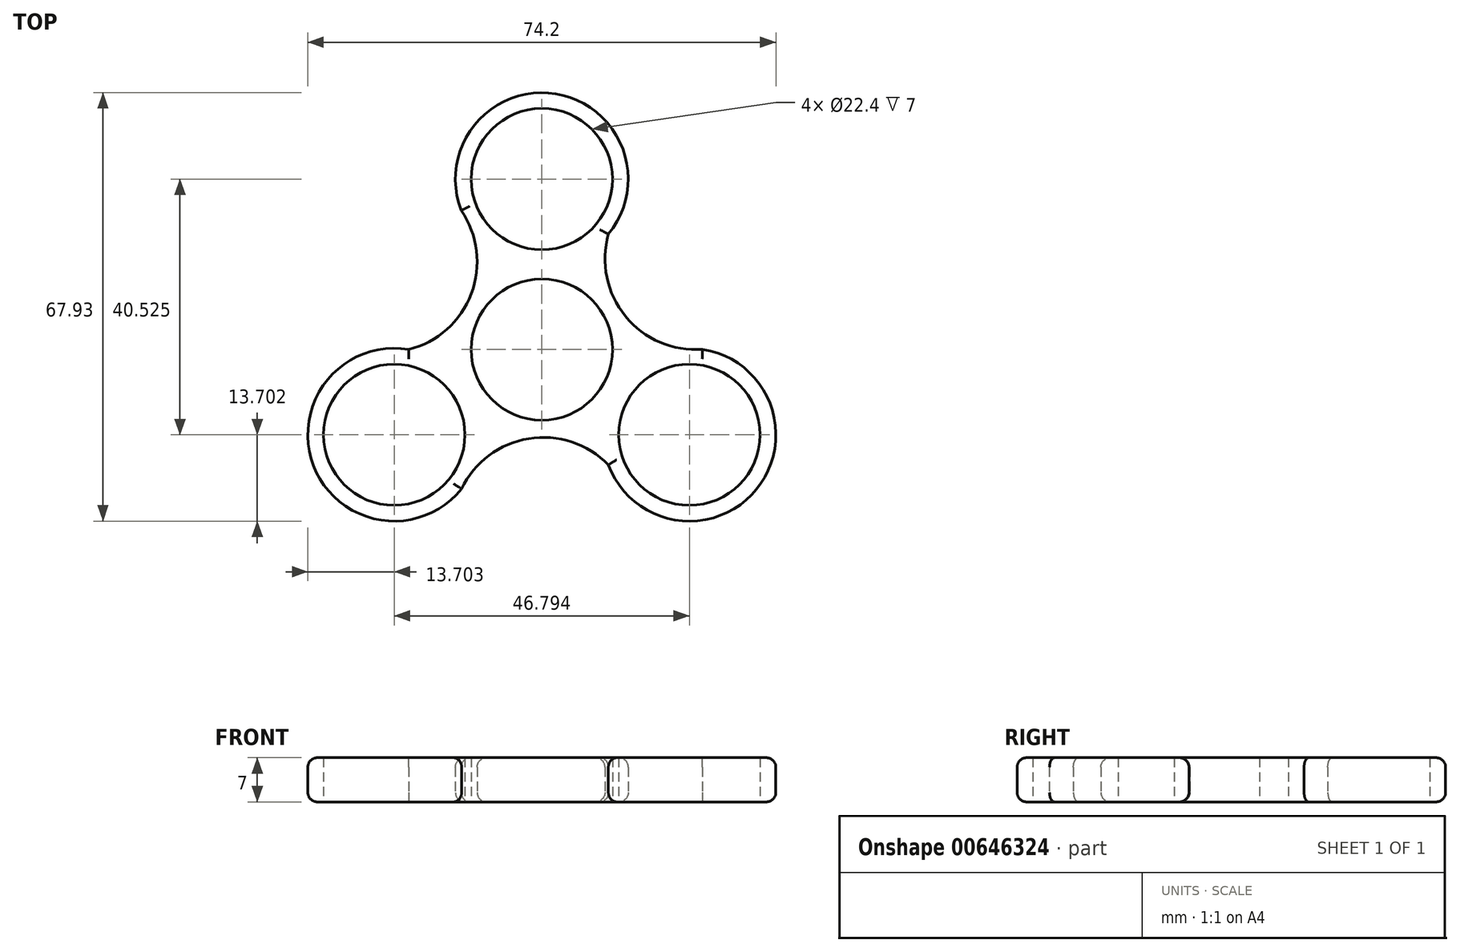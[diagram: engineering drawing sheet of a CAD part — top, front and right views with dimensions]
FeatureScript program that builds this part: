
annotation { "Feature Type Name" : "Feature", "Feature Type Description" : "" }
export const myFeature = defineFeature(function(context is Context, id is Id, definition is map)
    precondition{}
    {
        {
            var Q0;
            Q0=qCreatedBy(makeId("Top.planeOp"),FACE);
            var sketch = newSketch(context, id + "F0", { "sketchPlane" : qUnion([Q0])});
            skCircle(sketch, "E0", {"center": v(0, 0) * mm, "radius": 11.2 * mm});
            skCircle(sketch, "E1", {"center": v(0, 27.02) * mm, "radius": 11.2 * mm});
            skArc(sketch, "E2", {"start": v(10.56, 18.28) * mm, "mid": v(0.58, 40.7) * mm, "end": v(-11.26, 19.21) * mm});
            skCircle(sketch, "E3.1.0", {"center": v(-23.4, -13.5) * mm, "radius": 11.2 * mm});
            skArc(sketch, "E3.1.1", {"start": v(-21.11, 0) * mm, "mid": v(-35.54, -19.85) * mm, "end": v(-11, -19.36) * mm});
            skCircle(sketch, "E3.2.0", {"center": v(23.4, -13.5) * mm, "radius": 11.2 * mm});
            skArc(sketch, "E3.2.1", {"start": v(10.56, -18.28) * mm, "mid": v(34.96, -20.86) * mm, "end": v(22.27, 0.15) * mm});
            skArc(sketch, "E4", {"start": v(-21.11, 0) * mm, "mid": v(-11.18, 8.85) * mm, "end": v(-12.77, 22.05) * mm});
            skArc(sketch, "E5.1.0", {"start": v(10.56, -18.28) * mm, "mid": v(-2.07, -14.1) * mm, "end": v(-12.71, -22.08) * mm});
            skArc(sketch, "E5.2.0", {"start": v(10.56, 18.28) * mm, "mid": v(13.25, 5.26) * mm, "end": v(25.48, 0.03) * mm});
            skSolve(sketch);
        }
        {
            var Q0;
            Q0=makeQuery(id+"F0.imprint","IMPRINT",FACE,{"disambiguationData":[TD([[makeQuery(id+"F0.imprint","IMPRINT",EDGE,{"derivedFrom":sQuery(id+"F0.wireOp",EDGE,"E0")}),-1.0]])]});
            extrude(context, id + "F1", {"entities" : qUnion([Q0]), "depth" : 7 * mm, "offsetDistance" : 25 * mm});
        }
        {
            var Q0;
            Q0=makeQuery(id+"F1.opExtrude","CAP_EDGE",EDGE,{"disambiguationData":[OSD([sQuery(id+"F0.wireOp",EDGE,"E2")])],"isStart":false});
            var Q1;
            Q1=makeQuery(id+"F1.opExtrude","CAP_EDGE",EDGE,{"disambiguationData":[OSD([sQuery(id+"F0.wireOp",EDGE,"E5.2.0")])],"isStart":false});
            var Q2;
            Q2=makeQuery(id+"F1.opExtrude","CAP_EDGE",EDGE,{"disambiguationData":[OSD([sQuery(id+"F0.wireOp",EDGE,"E3.2.1")])],"isStart":false});
            var Q3;
            Q3=makeQuery(id+"F1.opExtrude","CAP_EDGE",EDGE,{"disambiguationData":[OSD([sQuery(id+"F0.wireOp",EDGE,"E5.1.0")])],"isStart":false});
            var Q4;
            Q4=makeQuery(id+"F1.opExtrude","CAP_EDGE",EDGE,{"disambiguationData":[OSD([sQuery(id+"F0.wireOp",EDGE,"E3.1.1")])],"isStart":false});
            var Q5;
            Q5=makeQuery(id+"F1.opExtrude","CAP_EDGE",EDGE,{"disambiguationData":[OSD([sQuery(id+"F0.wireOp",EDGE,"E4")])],"isStart":false});
            fillet(context, id + "F2", {"entities" : qUnion([Q0, Q1, Q2, Q3, Q4, Q5]), "radius" : 1.5 * mm, "tangentPropagation" : true, "allowEdgeOverflow" : false});
        }
        {
            var Q0;
            Q0=makeQuery(id+"F1.opExtrude","CAP_EDGE",EDGE,{"disambiguationData":[OSD([sQuery(id+"F0.wireOp",EDGE,"E3.2.1")])],"isStart":true});
            var Q1;
            Q1=makeQuery(id+"F1.opExtrude","CAP_EDGE",EDGE,{"disambiguationData":[OSD([sQuery(id+"F0.wireOp",EDGE,"E5.2.0")])],"isStart":true});
            var Q2;
            Q2=makeQuery(id+"F1.opExtrude","CAP_EDGE",EDGE,{"disambiguationData":[OSD([sQuery(id+"F0.wireOp",EDGE,"E2")])],"isStart":true});
            var Q3;
            Q3=makeQuery(id+"F1.opExtrude","CAP_EDGE",EDGE,{"disambiguationData":[OSD([sQuery(id+"F0.wireOp",EDGE,"E4")])],"isStart":true});
            var Q4;
            Q4=makeQuery(id+"F1.opExtrude","CAP_EDGE",EDGE,{"disambiguationData":[OSD([sQuery(id+"F0.wireOp",EDGE,"E3.1.1")])],"isStart":true});
            var Q5;
            Q5=makeQuery(id+"F1.opExtrude","CAP_EDGE",EDGE,{"disambiguationData":[OSD([sQuery(id+"F0.wireOp",EDGE,"E5.1.0")])],"isStart":true});
            fillet(context, id + "F3", {"entities" : qUnion([Q0, Q1, Q2, Q3, Q4, Q5]), "radius" : 1.5 * mm, "tangentPropagation" : true, "allowEdgeOverflow" : false});
        }
    });
